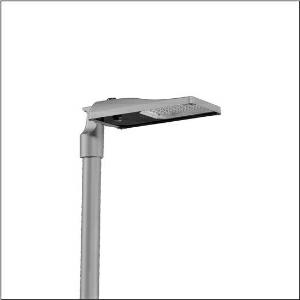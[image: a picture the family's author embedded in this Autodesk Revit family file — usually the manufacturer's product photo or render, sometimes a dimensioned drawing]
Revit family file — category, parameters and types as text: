
# Revit family: streetlight_sl_31_mini___p1_0a_5xh6a31t08ga_b1da
name_source: partatom
category: Lighting Fixtures
units: mm (PartAtom-declared; Revit-internal decimal feet)

## family parameters
Cut with Voids When Loaded = No
Host = Face
Light Source = No
Part Type = Normal
Room Calculation Point = No
Round Connector Dimension = Use Diameter
Shared = No

## types (1)
- --- (1 x LED, 5710 lm, 39.3 W, 3000K)
    Apparent Load = 39 VA
    CIE Flux Codes = 23 55 94 100 100
    Color Rendering = 70
    Color Temperature = 3000K
    Default Elevation = 1800 mm
    Description = Streetlight SL 31 mini D4i, Desk-Remote mast luminaire for post-top, side-entry; light control with lens of PMMA; light distribution: P1.0a, direct asymmetric distribution, for standard-compliant lighting for roads and squares; LED: luminous flux: 5.710lm, light colour: 730, colour temperature: 3000K; luminous efficacy: 145,3lm/W; control: pre-setting: logarithmic dimming characteristic, flexible luminous flux parameterisation, time-dependent luminous flux control, constant luminous flux control, power reduction, intelligent temperature release in ECG and LED module, overheat protection; luminaire housing, of diecast aluminium, Siteco® metallic grey (DB 702S), corrosivity category C5 high according to DIN EN ISO 12944; cover of toughened safety glass, transparent, opened without tools; mast flange of diecast aluminium, Siteco® metallic grey (DB 702S), spigot size: 76/60mm, mast flange included unmounted; with cable H07RN-F 2x 1.5mm², cable length: 6,5m, connection cable pre-assembled; mains connection: 220..240V, AC, 50/60Hz; power consumption (at start of service life): 39,3W / (at end of service life): 40,7W / (with reduced operation 50%): 18,1W; protection rating (complete): IP66; insulation class (complete): insulation class II (safety insulation); impact resistance: IK09; certification: CE, ENEC, ENEC+, VDE, UKCA, ZD4i; permissible operating ambient temperature for outdoor applications: -40..+50°C; packaging unit: 1 piece

Light Distribution: P1.0a
    Height = 76 mm
    Lamp = 1 x LED
    Lamp Light Flux = 5710 lm
    Lamp Power = 39.3 W
    Lamp count = 1
    Length = 547 mm
    Luminous efficacy = 145 lm/W
    Manufacturer = Siteco
    ModVariant = No
    Model = 5XH6A31T08GA
    Number of Poles = 1
    OnlyDefault = Yes
    Power Factor = 1
    Product Name = Streetlight SL 31 mini | P1.0a
    Product group = mast luminaire | pylon top
    ProductGroupID = 6100
    Protection Class = Protection class II
    Protection Degree = IP 66
    RLX_Detail_Level = 1
    RLX_Emergency_Light_Flux = 0 lm
    RLX_Emergency_Type = 0
    RLX_Emergency_Type_DB = No
    RlxData = <blob elided: 39501 chars, md5=80f44ae5>
    Socket = socket
    Standby Power = 0 W
    System Light Flux = 5710 lm
    System Power = 39 W
    Type Comments = factory setting: luminous flux: 100 % | dim-lin: 254 | 798 mA
    Type Image = l_1300332.jpg
    URL = http://relux.com
    VarID = @adj_078335
    Voltage = 0 V
    Weight = 0.00 kg
    Width = 265 mm

## geometry (parser evidence)
native form markers: Blend x4, Sweep x8
no freeform markers — native parametric forms only
